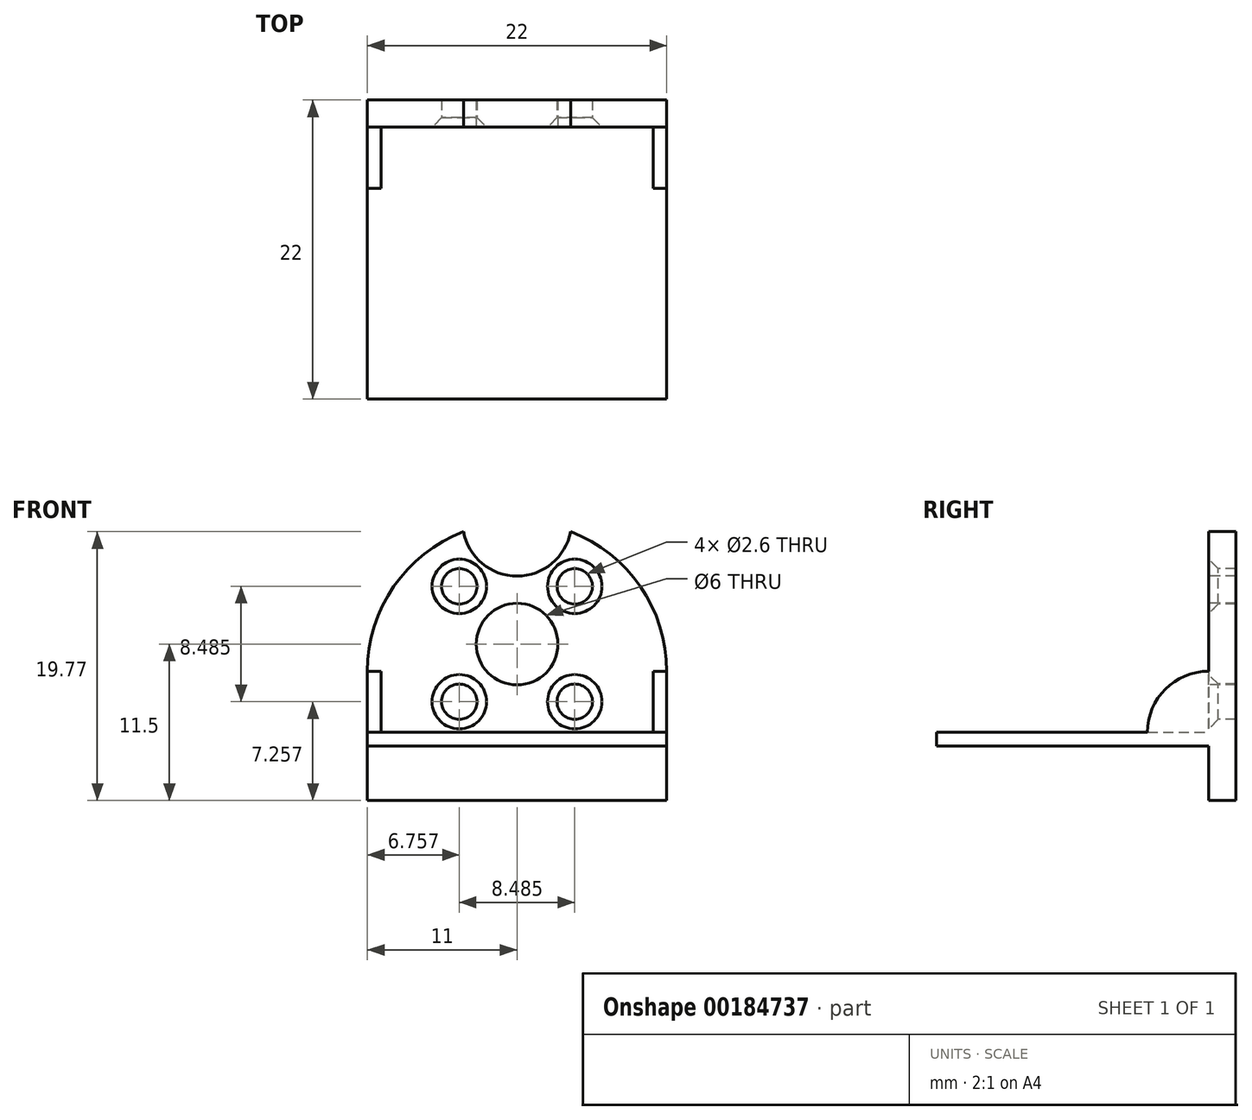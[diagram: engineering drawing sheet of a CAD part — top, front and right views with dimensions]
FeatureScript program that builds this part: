
annotation { "Feature Type Name" : "Feature", "Feature Type Description" : "" }
export const myFeature = defineFeature(function(context is Context, id is Id, definition is map)
    precondition{}
    {
        {
            var Q0;
            Q0=qCreatedBy(makeId("Front.planeOp"),FACE);
            var sketch = newSketch(context, id + "F0", { "sketchPlane" : qUnion([Q0])});
            skLineSegment(sketch, "E0", {"start": v(0, 0) * mm, "end": v(0, 6.5) * mm, "construction": true});
            skCircle(sketch, "E1", {"center": v(4.24, 2.26) * mm, "radius": 1.3 * mm});
            skLineSegment(sketch, "E2", {"start": v(0, 6.5) * mm, "end": v(4.24, 2.26) * mm, "construction": true});
            skCircle(sketch, "E3.1.0", {"center": v(-4.24, 2.26) * mm, "radius": 1.3 * mm});
            skCircle(sketch, "E3.2.0", {"center": v(-4.24, 10.74) * mm, "radius": 1.3 * mm});
            skCircle(sketch, "E3.3.0", {"center": v(4.24, 10.74) * mm, "radius": 1.3 * mm});
            skPoint(sketch, "E3.center", {"position": v(0, 6.5) * mm});
            skLineSegment(sketch, "E3.anchor2", {"start": v(0, 6.5) * mm, "end": v(4.24, 10.74) * mm, "construction": true});
            skCircle(sketch, "E4", {"center": v(0, 6.5) * mm, "radius": 3 * mm});
            skLineSegment(sketch, "E5.bottom", {"start": v(11, -5) * mm, "end": v(-11, -5) * mm});
            skLineSegment(sketch, "E5.top", {"start": v(0, 15.5) * mm, "end": v(0, 15.5) * mm});
            skLineSegment(sketch, "E5.left", {"start": v(11, -5) * mm, "end": v(11, 4.5) * mm});
            skLineSegment(sketch, "E5.right", {"start": v(-11, -5) * mm, "end": v(-11, 4.5) * mm});
            skPoint(sketch, "E5.middle", {"position": v(0, 5.25) * mm});
            skLineSegment(sketch, "E6.bottom", {"start": v(-11, 0) * mm, "end": v(11, 0) * mm});
            skLineSegment(sketch, "E6.top", {"start": v(-11, -1) * mm, "end": v(11, -1) * mm});
            skLineSegment(sketch, "E6.left", {"start": v(-11, 0) * mm, "end": v(-11, -1) * mm});
            skLineSegment(sketch, "E6.right", {"start": v(11, 0) * mm, "end": v(11, -1) * mm});
            skCircle(sketch, "E7", {"center": v(0, 6.5) * mm, "radius": 9 * mm, "construction": true});
            skPoint(sketch, "E8.visualSharp", {"position": v(-11, 15.5) * mm});
            skArc(sketch, "E8.filletArc", {"start": v(0, 15.5) * mm, "mid": v(-7.78, 12.28) * mm, "end": v(-11, 4.5) * mm});
            skPoint(sketch, "E9.visualSharp", {"position": v(11, 15.5) * mm});
            skArc(sketch, "E9.filletArc", {"start": v(11, 4.5) * mm, "mid": v(7.78, 12.28) * mm, "end": v(0, 15.5) * mm});
            skLineSegment(sketch, "E10.bottom", {"start": v(-11, 4.5) * mm, "end": v(-10, 4.5) * mm});
            skLineSegment(sketch, "E10.top", {"start": v(-11, 0) * mm, "end": v(-10, 0) * mm});
            skLineSegment(sketch, "E10.left", {"start": v(-11, 4.5) * mm, "end": v(-11, 0) * mm});
            skLineSegment(sketch, "E10.right", {"start": v(-10, 4.5) * mm, "end": v(-10, 0) * mm});
            skLineSegment(sketch, "E11.bottom", {"start": v(11, 4.5) * mm, "end": v(11, 4.5) * mm});
            skLineSegment(sketch, "E11.top", {"start": v(11, 0) * mm, "end": v(11, 0) * mm});
            skLineSegment(sketch, "E11.left", {"start": v(11, 4.5) * mm, "end": v(11, 0) * mm});
            skLineSegment(sketch, "E11.right", {"start": v(11, 4.5) * mm, "end": v(11, 0) * mm});
            skLineSegment(sketch, "E12.bottom", {"start": v(11, 4.5) * mm, "end": v(10, 4.5) * mm});
            skLineSegment(sketch, "E12.top", {"start": v(11, 0) * mm, "end": v(10, 0) * mm});
            skLineSegment(sketch, "E12.right", {"start": v(10, 4.5) * mm, "end": v(10, 0) * mm});
            skLineSegment(sketch, "E13", {"start": v(-3, 6.5) * mm, "end": v(3, 6.5) * mm, "construction": true});
            skArc(sketch, "E14", {"start": v(3.93, 14.77) * mm, "mid": v(0, 11.5) * mm, "end": v(-3.93, 14.77) * mm});
            skSolve(sketch);
        }
        {
            var Q0;
            Q0=makeQuery(id+"F0.imprint","IMPRINT",FACE,{"disambiguationData":[TD([[makeQuery(id+"F0.imprint","IMPRINT",EDGE,{"derivedFrom":sQuery(id+"F0.wireOp",EDGE,"E1")}),-1.0]])]});
            var Q1;
            {var subQ0=sQuery(id+"F0.wireOp",EDGE,"E5.bottom");Q1=makeQuery(id+"F0.imprint","IMPRINT",FACE,{"disambiguationData":[TD([[makeQuery(id+"F0.imprint","IMPRINT",EDGE,{"derivedFrom":subQ0}),-1.0]])]});}
            var Q2;
            Q2=makeQuery(id+"F0.imprint","IMPRINT",FACE,{"disambiguationData":[TD([[makeQuery(id+"F0.imprint","IMPRINT",EDGE,{"derivedFrom":sQuery(id+"F0.wireOp",EDGE,"E6.bottom")}),-1.0]])]});
            var Q3;
            Q3=makeQuery(id+"F0.imprint","IMPRINT",FACE,{"disambiguationData":[TD([[makeQuery(id+"F0.imprint","IMPRINT",EDGE,{"derivedFrom":sQuery(id+"F0.wireOp",EDGE,"E10.bottom")}),-1.0]])]});
            var Q4;
            Q4=makeQuery(id+"F0.imprint","IMPRINT",FACE,{"disambiguationData":[TD([[makeQuery(id+"F0.imprint","IMPRINT",EDGE,{"derivedFrom":sQuery(id+"F0.wireOp",EDGE,"E12.bottom")}),1.0]])]});
            extrude(context, id + "F1", {"entities" : qUnion([Q0, Q1, Q2, Q3, Q4]), "oppositeDirection" : true, "depth" : 2 * mm});
        }
        {
            var Q0;
            Q0=makeQuery(id+"F0.imprint","IMPRINT",FACE,{"disambiguationData":[TD([[makeQuery(id+"F0.imprint","IMPRINT",EDGE,{"derivedFrom":sQuery(id+"F0.wireOp",EDGE,"E6.bottom")}),-1.0]])]});
            extrude(context, id + "F2", {"entities" : qUnion([Q0]), "depth" : 20 * mm});
        }
        {
            var Q0;
            Q0=makeQuery(id+"F0.imprint","IMPRINT",FACE,{"disambiguationData":[TD([[makeQuery(id+"F0.imprint","IMPRINT",EDGE,{"derivedFrom":sQuery(id+"F0.wireOp",EDGE,"E10.bottom")}),-1.0]])]});
            var Q1;
            Q1=makeQuery(id+"F0.imprint","IMPRINT",FACE,{"disambiguationData":[TD([[makeQuery(id+"F0.imprint","IMPRINT",EDGE,{"derivedFrom":sQuery(id+"F0.wireOp",EDGE,"E12.bottom")}),1.0]])]});
            var Q2;
            Q2=makeQuery(id+"F2.opExtrude","CAP_EDGE",EDGE,{"disambiguationData":[OSD([sQuery(id+"F0.wireOp",EDGE,"E6.bottom"),sQuery(id+"F0.wireOp",EDGE,"E10.top"),sQuery(id+"F0.wireOp",EDGE,"E12.top")])],"isStart":true});
            revolve(context, id + "F3", {"operationType" : NewBodyOperationType.ADD, "entities" : qUnion([Q0, Q1]), "axis" : qUnion([Q2]), "revolveType" : RevolveType.ONE_DIRECTION, "angle" : 91 * degree});
        }
        {
            var Q0;
            Q0=sQuery(id+"F0.wireOp",VERTEX,"E3.2.0.center");
            var Q1;
            Q1=sQuery(id+"F0.wireOp",VERTEX,"E3.1.0.center");
            var Q2;
            Q2=sQuery(id+"F0.wireOp",VERTEX,"E1.center");
            var Q3;
            Q3=sQuery(id+"F0.wireOp",VERTEX,"E3.3.0.center");
            var Q4;
            Q4=makeQuery(id+"F1.opExtrude","SWEPT_BODY",BODY,{"disambiguationData":[OSD([sQuery(id+"F0.wireOp",EDGE,"E1"),sQuery(id+"F0.wireOp",EDGE,"E3.1.0"),sQuery(id+"F0.wireOp",EDGE,"E3.2.0"),sQuery(id+"F0.wireOp",EDGE,"E3.3.0"),sQuery(id+"F0.wireOp",EDGE,"E4"),sQuery(id+"F0.wireOp",EDGE,"E5.bottom"),sQuery(id+"F0.wireOp",EDGE,"E5.left"),sQuery(id+"F0.wireOp",EDGE,"E5.right"),sQuery(id+"F0.wireOp",EDGE,"E6.left"),sQuery(id+"F0.wireOp",EDGE,"E6.right"),sQuery(id+"F0.wireOp",EDGE,"E8.filletArc"),sQuery(id+"F0.wireOp",EDGE,"E9.filletArc"),sQuery(id+"F0.wireOp",EDGE,"E10.left"),sQuery(id+"F0.wireOp",EDGE,"E11.left")])]});
            hole(context, id + "F4", {"style" : HoleStyle.C_SINK, "endStyle" : HoleEndStyle.BLIND, "holeDiameter" : 2 * mm, "cSinkDiameter" : 4 * mm, "cSinkAngle" : 90 * degree, "holeDepth" : 3 * mm, "locations" : qUnion([Q0, Q1, Q2, Q3]), "scope" : qUnion([Q4])});
        }
    });
